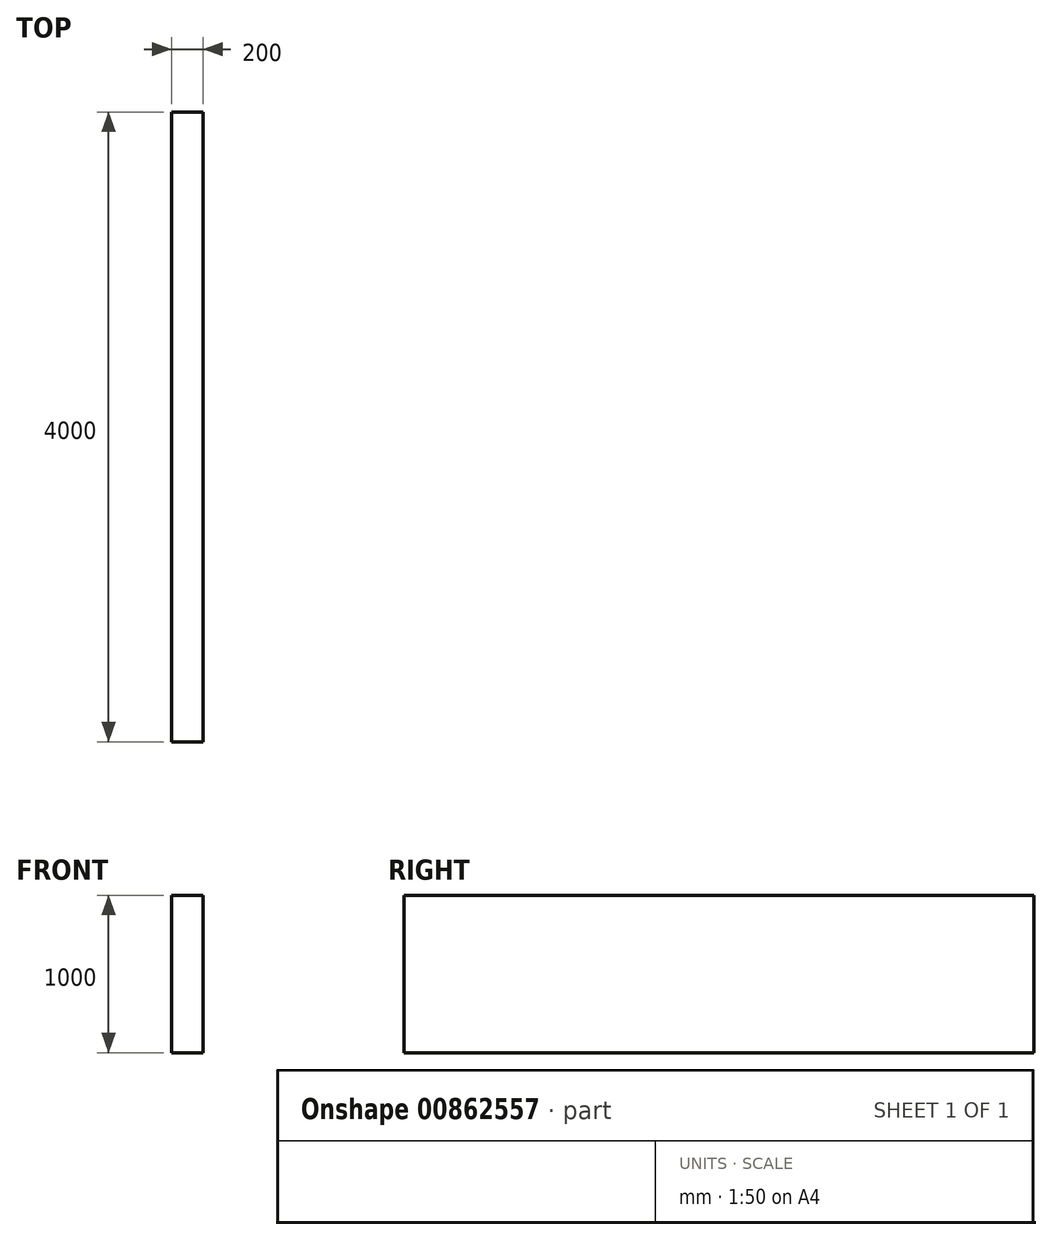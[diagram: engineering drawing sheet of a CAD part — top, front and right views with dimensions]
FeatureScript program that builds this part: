
annotation { "Feature Type Name" : "Feature", "Feature Type Description" : "" }
export const myFeature = defineFeature(function(context is Context, id is Id, definition is map)
    precondition{}
    {
        {
            var Q0;
            Q0=qCreatedBy(makeId("Front.planeOp"),FACE);
            var sketch = newSketch(context, id + "F0", { "sketchPlane" : qUnion([Q0])});
            skLineSegment(sketch, "E0.bottom", {"start": v(-200, 1000) * mm, "end": v(0, 1000) * mm});
            skLineSegment(sketch, "E0.top", {"start": v(-200, 0) * mm, "end": v(0, 0) * mm});
            skLineSegment(sketch, "E0.left", {"start": v(-200, 1000) * mm, "end": v(-200, 0) * mm});
            skLineSegment(sketch, "E0.right", {"start": v(0, 1000) * mm, "end": v(0, 0) * mm});
            skSolve(sketch);
        }
        {
            var Q0;
            Q0=makeQuery(id+"F0.imprint","IMPRINT",FACE,{"disambiguationData":[TD([[makeQuery(id+"F0.imprint","IMPRINT",EDGE,{"derivedFrom":sQuery(id+"F0.wireOp",EDGE,"E0.bottom")}),-1.0]])]});
            extrude(context, id + "F1", {"entities" : qUnion([Q0]), "depth" : 4000 * mm, "offsetDistance" : 25 * mm});
        }
    });
